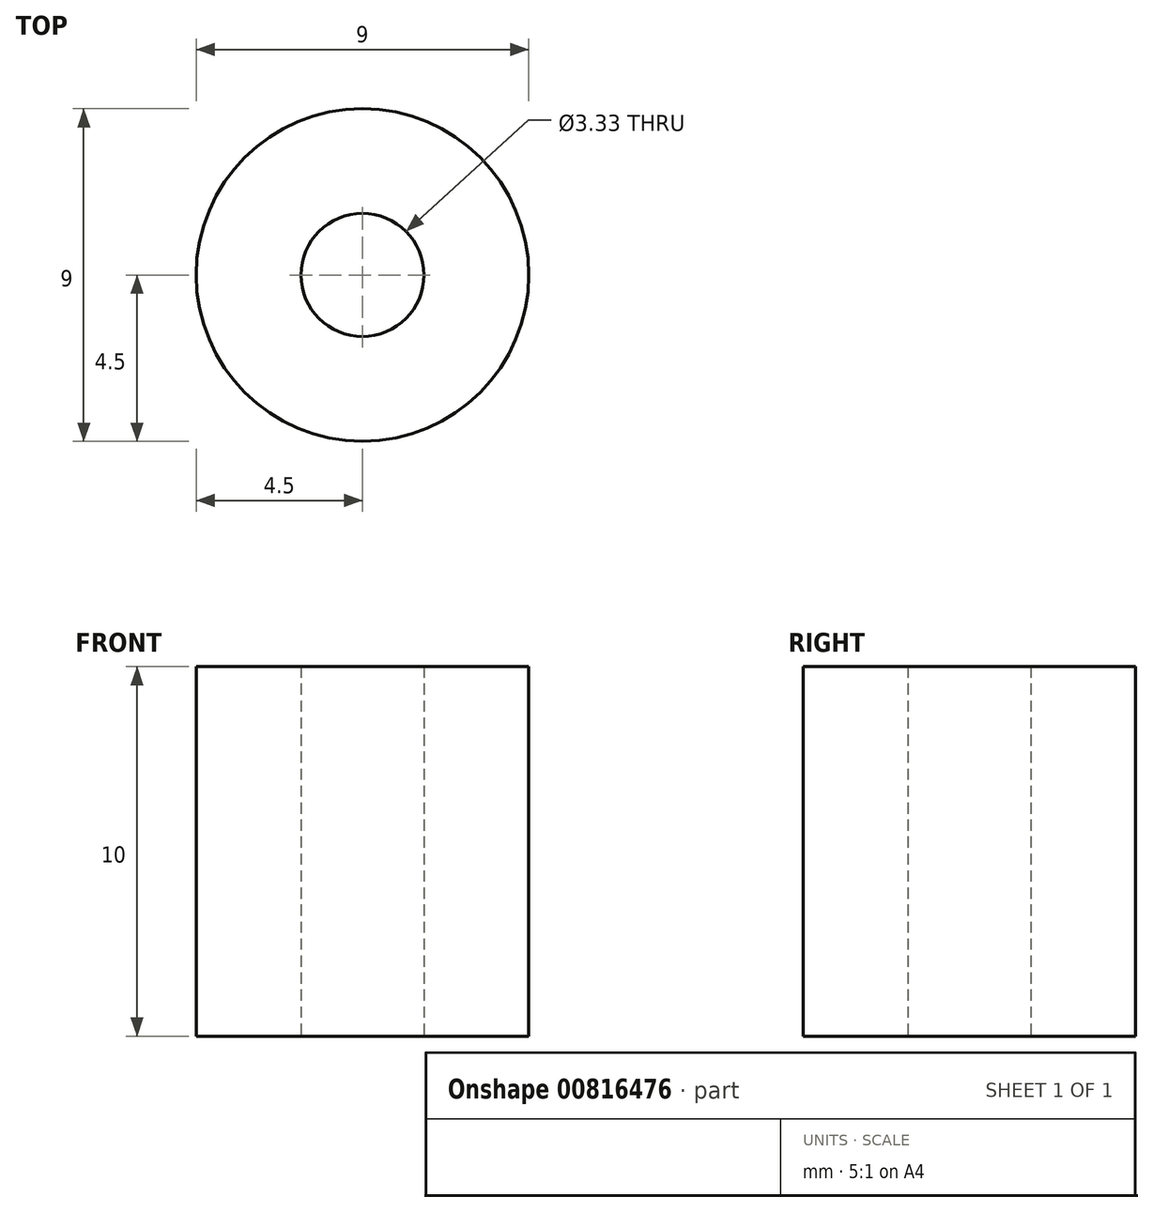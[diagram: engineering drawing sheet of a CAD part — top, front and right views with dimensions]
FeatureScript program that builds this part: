
annotation { "Feature Type Name" : "Feature", "Feature Type Description" : "" }
export const myFeature = defineFeature(function(context is Context, id is Id, definition is map)
    precondition{}
    {
        {
            var Q0;
            Q0=qCreatedBy(makeId("Top.planeOp"),FACE);
            var sketch = newSketch(context, id + "F0", { "sketchPlane" : qUnion([Q0])});
            skCircle(sketch, "E0", {"center": v(0, 0) * mm, "radius": 1.67 * mm});
            skCircle(sketch, "E1", {"center": v(0, 0) * mm, "radius": 4.5 * mm});
            skSolve(sketch);
        }
        {
            var Q0;
            Q0=makeQuery(id+"F0.imprint","IMPRINT",FACE,{"disambiguationData":[TD([[makeQuery(id+"F0.imprint","IMPRINT",EDGE,{"derivedFrom":sQuery(id+"F0.wireOp",EDGE,"E0")}),-1.0]])]});
            extrude(context, id + "F1", {"entities" : qUnion([Q0]), "depth" : 10 * mm, "offsetDistance" : 25 * mm});
        }
    });
